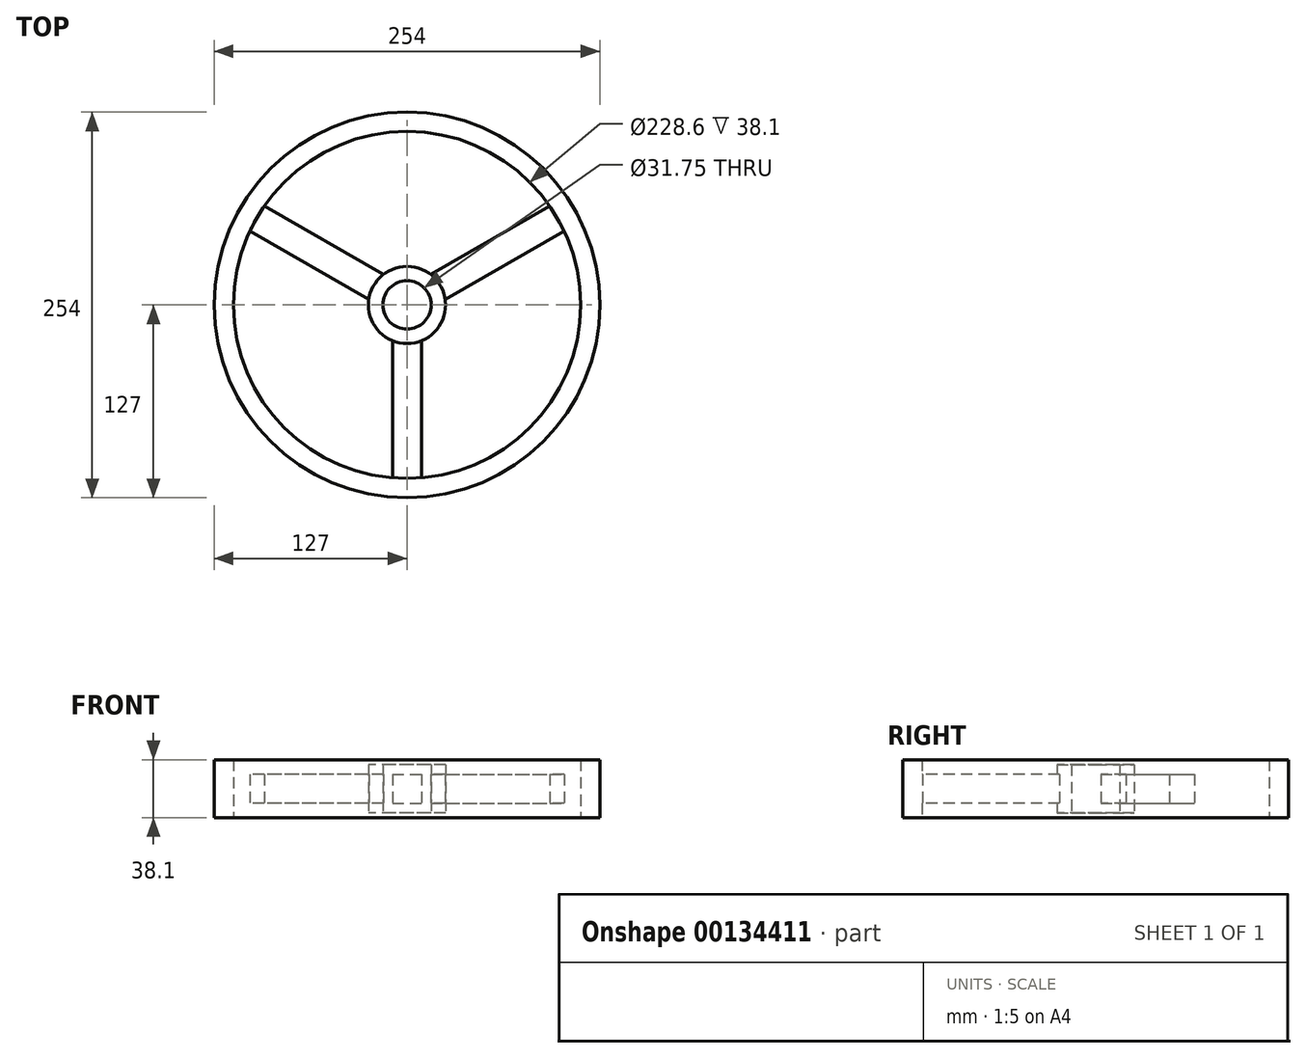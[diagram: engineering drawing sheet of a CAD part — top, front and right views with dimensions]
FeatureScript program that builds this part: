
annotation { "Feature Type Name" : "Feature", "Feature Type Description" : "" }
export const myFeature = defineFeature(function(context is Context, id is Id, definition is map)
    precondition{}
    {
        {
            var Q0;
            Q0=qCreatedBy(makeId("Top.planeOp"),FACE);
            var sketch = newSketch(context, id + "F0", { "sketchPlane" : qUnion([Q0])});
            skCircle(sketch, "E0", {"center": v(0, 0) * mm, "radius": 127 * mm});
            skCircle(sketch, "E1", {"center": v(0, 0) * mm, "radius": 114.3 * mm});
            skCircle(sketch, "E2", {"center": v(0, 0) * mm, "radius": 25.4 * mm});
            skCircle(sketch, "E3", {"center": v(0, 0) * mm, "radius": 15.88 * mm});
            skLineSegment(sketch, "E4", {"start": v(0, 0) * mm, "end": v(0, -19.05) * mm});
            skLineSegment(sketch, "E5", {"start": v(4.44, -19.05) * mm, "end": v(-4.44, -19.05) * mm});
            skLineSegment(sketch, "E6", {"start": v(4.44, -19.05) * mm, "end": v(4.44, -15.24) * mm});
            skLineSegment(sketch, "E7", {"start": v(-4.44, -19.05) * mm, "end": v(-4.44, -15.24) * mm});
            skLineSegment(sketch, "E8", {"start": v(9.52, -23.55) * mm, "end": v(9.52, -113.9) * mm});
            skLineSegment(sketch, "E9", {"start": v(-9.52, -23.55) * mm, "end": v(-9.52, -113.9) * mm});
            skLineSegment(sketch, "E10", {"start": v(0, -25.4) * mm, "end": v(0, -114.3) * mm, "construction": true});
            skSolve(sketch);
        }
        {
            var Q0;
            Q0=makeQuery(id+"F0.imprint","IMPRINT",FACE,{"disambiguationData":[TD([[makeQuery(id+"F0.imprint","IMPRINT",EDGE,{"derivedFrom":sQuery(id+"F0.wireOp",EDGE,"E0")}),1.0]])]});
            extrude(context, id + "F1", {"entities" : qUnion([Q0]), "endBound" : BoundingType.SYMMETRIC, "depth" : 38.1 * mm});
        }
        {
            var Q0;
            {var subQ0=sQuery(id+"F0.wireOp",EDGE,"E8");Q0=makeQuery(id+"F0.imprint","IMPRINT",FACE,{"disambiguationData":[TD([[makeQuery(id+"F0.imprint","IMPRINT",EDGE,{"derivedFrom":subQ0}),-1.0]])]});}
            extrude(context, id + "F2", {"entities" : qUnion([Q0]), "endBound" : BoundingType.SYMMETRIC, "depth" : 19.05 * mm});
        }
        {
            var Q0;
            {var subQ0=sQuery(id+"F0.wireOp",EDGE,"E6");Q0=makeQuery(id+"F0.imprint","IMPRINT",FACE,{"disambiguationData":[TD([[makeQuery(id+"F0.imprint","IMPRINT",EDGE,{"derivedFrom":subQ0}),-1.0]])]});}
            extrude(context, id + "F3", {"entities" : qUnion([Q0]), "operationType" : NewBodyOperationType.ADD, "endBound" : BoundingType.SYMMETRIC, "depth" : 31.75 * mm});
        }
        {
            var Q0;
            Q0=makeQuery(id+"F2.opExtrude","SWEPT_BODY",BODY,{"disambiguationData":[OSD([sQuery(id+"F0.wireOp",EDGE,"E1"),sQuery(id+"F0.wireOp",EDGE,"E2"),sQuery(id+"F0.wireOp",EDGE,"E8"),sQuery(id+"F0.wireOp",EDGE,"E9")])]});
            var Q1;
            Q1=makeQuery(id+"F3.opExtrude","SWEPT_FACE",FACE,{"disambiguationData":[OSD([sQuery(id+"F0.wireOp",EDGE,"E2")])]});
            circularPattern(context, id + "F4", {"operationType" : NewBodyOperationType.ADD, "entities" : qUnion([Q0]), "axis" : qUnion([Q1]), "angle" : 120 * degree, "instanceCount" : 3});
        }
    });
